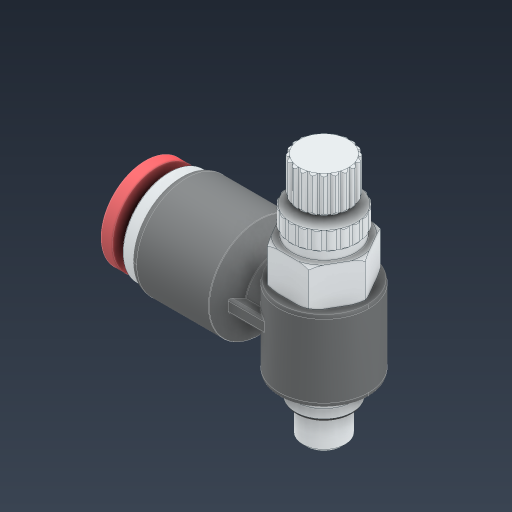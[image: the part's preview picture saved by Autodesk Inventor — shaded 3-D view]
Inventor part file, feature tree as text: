
AUTODESK INVENTOR PART (.ipt)
format: ipt  version: 2024.3 (Build 283343000, 343)  size: 841,216 bytes
history: native  units: in
note: dims shown in document units (in); Inventor stores cm internally (conversion verified against a paired STEP export)
features: other x4, pattern_circular x2, revolve x1, chamfer x1
ambient origin geometry x8: Origin, YZ Plane, XZ Plane, XY Plane, X Axis, Y Axis, Z Axis, Center Point
bodies: Solid1 (feature_tree), Solid2 (feature_tree), Solid3 (feature_tree), Solid4 (feature_tree), Solid5 (feature_tree), Solid6 (feature_tree), Solid7 (feature_tree)
feature tree (8):
  other  "Air Flow Valve Fitting1"
  revolve  "Revolve2"  [1 undecoded]
  other  "_276-8639-002 Rev1_-_Fillet2_"
  other  "_276-8639-002 Rev1_-_Fillet4_"
  parser-record x1  (decoder bookkeeping rows leaked as tree rows — omitted from the tree; the rows remain in map.json)
  chamfer  "Chamfer3"  [1 undecoded]
  pattern_circular  "CirPattern1"
  pattern_circular  "CirPattern2"
note: 2 required parameter values undecoded (feature->parameter linkage not recoverable at this tier; creation-order binding heuristic only, values carry confidence <= 0.55)
